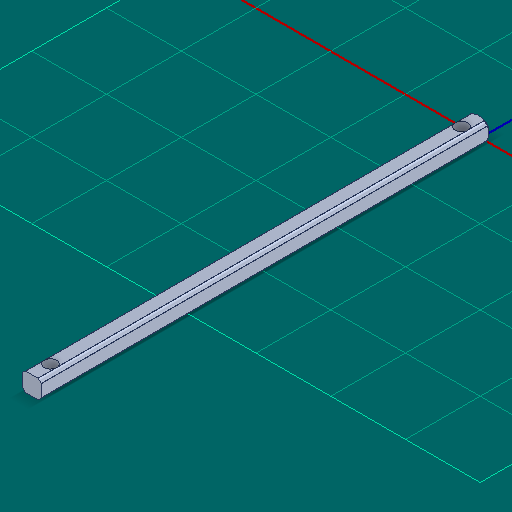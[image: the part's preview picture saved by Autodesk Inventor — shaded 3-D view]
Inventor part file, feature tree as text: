
AUTODESK INVENTOR PART (.ipt)
format: ipt  version: 2025 (Build 290162000, 162)  size: 189,440 bytes
history: native  units: in
note: dims shown in document units (in); Inventor stores cm internally (conversion verified against a paired STEP export)
features: extrude x3, sketch x3, thicken_offset x1, other x1
ambient origin geometry x8: Origin, YZ Plane, XZ Plane, XY Plane, X Axis, Y Axis, Z Axis, Center Point
bodies: Solid1 (feature_tree)
feature tree (8):
  extrude  "Extrusion1"  Depth=12.1875in
  thicken_offset  "Thicken1"
  extrude  "Extrusion2"  Depth=18.125in
  extrude  "Extrusion3"  Depth=0.172in
  sketch  "Sketch2"  dims[d0=0.0625in d1=0.0in d2=12.1875in]
  sketch  "Sketch3"  dims[d3=12.125in d4=18.125in]
  sketch  "Sketch4"  dims[d5=0.0in d6=0.172in d7=0.172in d8=1.0in d9=0.0in]
  other  "Cut-Revolve3"
